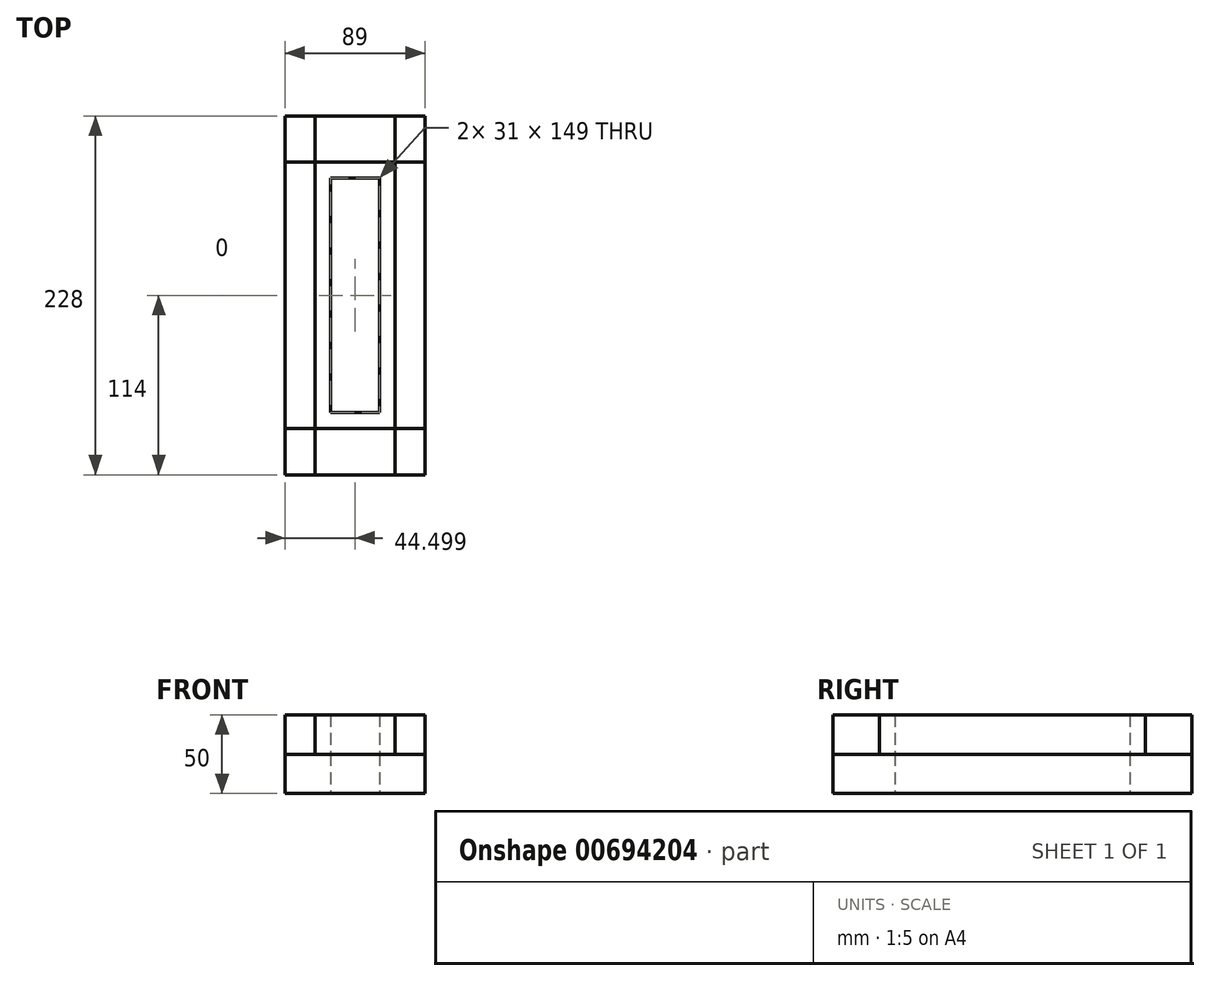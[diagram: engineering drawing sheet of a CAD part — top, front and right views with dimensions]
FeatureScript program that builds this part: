
annotation { "Feature Type Name" : "Feature", "Feature Type Description" : "" }
export const myFeature = defineFeature(function(context is Context, id is Id, definition is map)
    precondition{}
    {
        {
            var Q0;
            Q0=qCreatedBy(makeId("Top.planeOp"),FACE);
            var sketch = newSketch(context, id + "F0", { "sketchPlane" : qUnion([Q0])});
            skLineSegment(sketch, "E0.bottom", {"start": v(-21.04, -39.5) * mm, "end": v(67.96, -39.5) * mm});
            skLineSegment(sketch, "E0.top", {"start": v(-21.04, 188.5) * mm, "end": v(67.96, 188.5) * mm});
            skLineSegment(sketch, "E0.left", {"start": v(-21.04, -39.5) * mm, "end": v(-21.04, 188.5) * mm});
            skLineSegment(sketch, "E0.right", {"start": v(67.96, -39.5) * mm, "end": v(67.96, 188.5) * mm});
            skPoint(sketch, "E1", {"position": v(23.46, 188.5) * mm});
            skPoint(sketch, "E2", {"position": v(-21.04, 74.5) * mm});
            skPoint(sketch, "E3", {"position": v(-86.88, 282.73) * mm});
            skLineSegment(sketch, "E4.bottom", {"start": v(7.96, 149) * mm, "end": v(38.96, 149) * mm});
            skLineSegment(sketch, "E4.top", {"start": v(7.96, 0) * mm, "end": v(38.96, 0) * mm});
            skLineSegment(sketch, "E4.left", {"start": v(7.96, 149) * mm, "end": v(7.96, 0) * mm});
            skLineSegment(sketch, "E4.right", {"start": v(38.96, 149) * mm, "end": v(38.96, 0) * mm});
            skPoint(sketch, "E5", {"position": v(23.46, 149) * mm});
            skPoint(sketch, "E6", {"position": v(7.96, 74.5) * mm});
            skSolve(sketch);
        }
        {
            var Q0;
            Q0=makeQuery(id+"F0.imprint","IMPRINT",FACE,{"disambiguationData":[TD([[makeQuery(id+"F0.imprint","IMPRINT",EDGE,{"derivedFrom":sQuery(id+"F0.wireOp",EDGE,"E0.bottom")}),1.0]])]});
            extrude(context, id + "F1", {"entities" : qUnion([Q0]), "depth" : 25 * mm, "offsetDistance" : 25 * mm});
        }
        {
            var Q0;
            Q0=makeQuery(id+"F1.opExtrude","CAP_FACE",FACE,{"disambiguationData":[OSD([sQuery(id+"F0.wireOp",EDGE,"E0.bottom"),sQuery(id+"F0.wireOp",EDGE,"E0.top"),sQuery(id+"F0.wireOp",EDGE,"E0.left"),sQuery(id+"F0.wireOp",EDGE,"E0.right"),sQuery(id+"F0.wireOp",EDGE,"E4.bottom"),sQuery(id+"F0.wireOp",EDGE,"E4.top"),sQuery(id+"F0.wireOp",EDGE,"E4.left"),sQuery(id+"F0.wireOp",EDGE,"E4.right")])],"isStart":false});
            var sketch = newSketch(context, id + "F2", { "sketchPlane" : qUnion([Q0])});
            skLineSegment(sketch, "E7.0", {"start": v(7.96, 149) * mm, "end": v(7.96, 0) * mm});
            skLineSegment(sketch, "E8.0", {"start": v(7.96, 149) * mm, "end": v(38.96, 149) * mm});
            skLineSegment(sketch, "E9.0", {"start": v(38.96, 149) * mm, "end": v(38.96, 0) * mm});
            skLineSegment(sketch, "E10.0", {"start": v(7.96, 0) * mm, "end": v(38.96, 0) * mm});
            skLineSegment(sketch, "E11.0", {"start": v(-2.04, 159) * mm, "end": v(-2.04, -10) * mm});
            skLineSegment(sketch, "E11.1", {"start": v(-2.04, 159) * mm, "end": v(48.96, 159) * mm});
            skLineSegment(sketch, "E11.2", {"start": v(48.96, 159) * mm, "end": v(48.96, -10) * mm});
            skLineSegment(sketch, "E11.3", {"start": v(-2.04, -10) * mm, "end": v(48.96, -10) * mm});
            skLineSegment(sketch, "E12.bottom", {"start": v(-2.04, 159) * mm, "end": v(-21.04, 159) * mm});
            skLineSegment(sketch, "E12.top", {"start": v(-2.04, 188.5) * mm, "end": v(-21.04, 188.5) * mm});
            skLineSegment(sketch, "E12.left", {"start": v(-2.04, 159) * mm, "end": v(-2.04, 188.5) * mm});
            skLineSegment(sketch, "E12.right", {"start": v(-21.04, 159) * mm, "end": v(-21.04, 188.5) * mm});
            skLineSegment(sketch, "E13.bottom", {"start": v(48.96, 159) * mm, "end": v(67.96, 159) * mm});
            skLineSegment(sketch, "E13.top", {"start": v(48.96, 188.5) * mm, "end": v(67.96, 188.5) * mm});
            skLineSegment(sketch, "E13.left", {"start": v(48.96, 159) * mm, "end": v(48.96, 188.5) * mm});
            skLineSegment(sketch, "E13.right", {"start": v(67.96, 159) * mm, "end": v(67.96, 188.5) * mm});
            skLineSegment(sketch, "E14.bottom", {"start": v(-2.04, -10) * mm, "end": v(-21.04, -10) * mm});
            skLineSegment(sketch, "E14.top", {"start": v(-2.04, -39.5) * mm, "end": v(-21.04, -39.5) * mm});
            skLineSegment(sketch, "E14.left", {"start": v(-2.04, -10) * mm, "end": v(-2.04, -39.5) * mm});
            skLineSegment(sketch, "E14.right", {"start": v(-21.04, -10) * mm, "end": v(-21.04, -39.5) * mm});
            skLineSegment(sketch, "E15.bottom", {"start": v(48.96, -10) * mm, "end": v(67.96, -10) * mm});
            skLineSegment(sketch, "E15.top", {"start": v(48.96, -39.5) * mm, "end": v(67.96, -39.5) * mm});
            skLineSegment(sketch, "E15.left", {"start": v(48.96, -10) * mm, "end": v(48.96, -39.5) * mm});
            skLineSegment(sketch, "E15.right", {"start": v(67.96, -10) * mm, "end": v(67.96, -39.5) * mm});
            skSolve(sketch);
        }
        {
            var Q0;
            Q0 = qSketchRegion(id + "F2", true);
            extrude(context, id + "F3", {"entities" : qUnion([Q0]), "depth" : 25 * mm, "offsetDistance" : 25 * mm});
        }
    });
